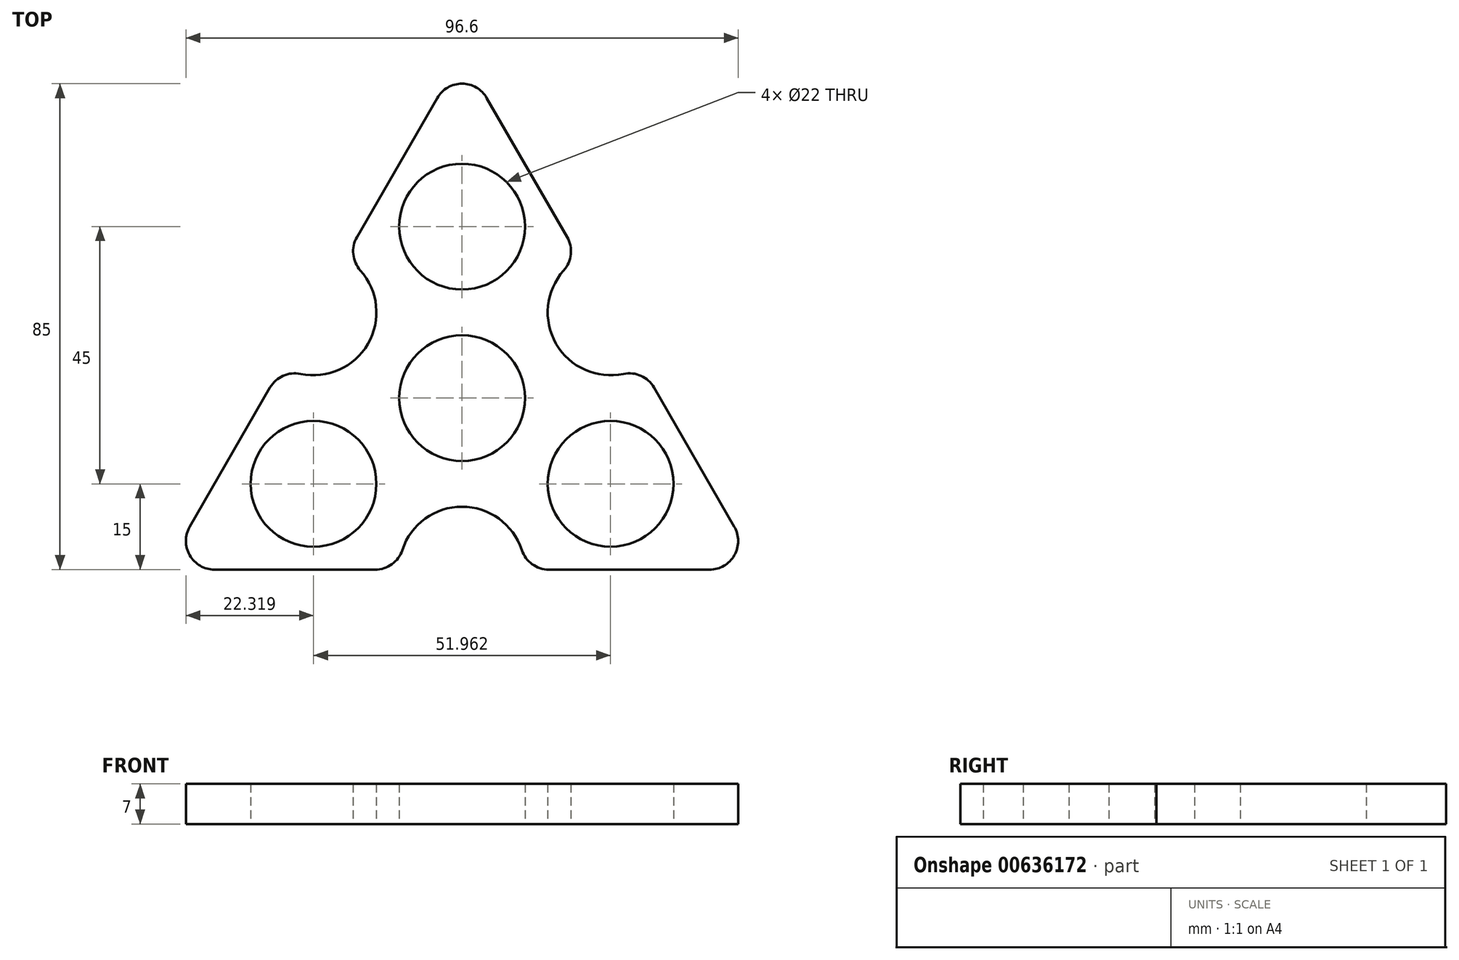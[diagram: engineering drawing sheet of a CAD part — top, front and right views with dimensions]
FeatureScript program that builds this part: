
annotation { "Feature Type Name" : "Feature", "Feature Type Description" : "" }
export const myFeature = defineFeature(function(context is Context, id is Id, definition is map)
    precondition{}
    {
        {
            var Q0;
            Q0=qCreatedBy(makeId("Top.planeOp"),FACE);
            var sketch = newSketch(context, id + "F0", { "sketchPlane" : qUnion([Q0])});
            skCircle(sketch, "E0", {"center": v(0, 0) * mm, "radius": 11 * mm});
            skCircle(sketch, "E1", {"center": v(0, 30) * mm, "radius": 11 * mm});
            skArc(sketch, "E2.1.0", {"start": v(-31.48, 5.47) * mm, "mid": v(-16.45, 9.5) * mm, "end": v(-20.48, 24.53) * mm});
            skCircle(sketch, "E2.2.0", {"center": v(-25.98, -15) * mm, "radius": 11 * mm});
            skArc(sketch, "E2.3.0", {"start": v(11, -30) * mm, "mid": v(0, -19) * mm, "end": v(-11, -30) * mm});
            skCircle(sketch, "E2.4.0", {"center": v(25.98, -15) * mm, "radius": 11 * mm});
            skArc(sketch, "E2.5.0", {"start": v(20.48, 24.53) * mm, "mid": v(16.45, 9.5) * mm, "end": v(31.48, 5.47) * mm});
            skLineSegment(sketch, "E3", {"start": v(-20.48, 24.53) * mm, "end": v(0, 60) * mm});
            skLineSegment(sketch, "E4", {"start": v(0, 60) * mm, "end": v(-20.48, 24.53) * mm});
            skLineSegment(sketch, "E5", {"start": v(0, 60) * mm, "end": v(20.48, 24.53) * mm});
            skLineSegment(sketch, "E6", {"start": v(-51.96, -30) * mm, "end": v(-11, -30) * mm});
            skLineSegment(sketch, "E7.trimOffspring", {"start": v(-31.48, 5.47) * mm, "end": v(-51.96, -30) * mm});
            skLineSegment(sketch, "E8.trimOffspring", {"start": v(31.48, 5.47) * mm, "end": v(51.96, -30) * mm});
            skLineSegment(sketch, "E9.trimOffspring", {"start": v(11, -30) * mm, "end": v(51.96, -30) * mm});
            skSolve(sketch);
        }
        {
            var Q0;
            Q0 = qSketchRegion(id + "F0", true);
            extrude(context, id + "F1", {"entities" : qUnion([Q0]), "depth" : 7 * mm, "offsetDistance" : 25 * mm});
        }
        {
            var Q0;
            Q0=makeQuery(id+"F1.opExtrude","SWEPT_EDGE",EDGE,{"disambiguationData":[OSD([sQuery(id+"F0.wireOp",EDGE,"E6"),sQuery(id+"F0.wireOp",EDGE,"E7.trimOffspring")])]});
            var Q1;
            Q1=makeQuery(id+"F1.opExtrude","SWEPT_EDGE",EDGE,{"disambiguationData":[OSD([sQuery(id+"F0.wireOp",EDGE,"E8.trimOffspring"),sQuery(id+"F0.wireOp",EDGE,"E9.trimOffspring")])]});
            var Q2;
            Q2=makeQuery(id+"F1.opExtrude","SWEPT_EDGE",EDGE,{"disambiguationData":[OSD([sQuery(id+"F0.wireOp",EDGE,"E4"),sQuery(id+"F0.wireOp",EDGE,"E5")])]});
            var Q3;
            Q3=makeQuery(id+"F1.opExtrude","SWEPT_EDGE",EDGE,{"disambiguationData":[OSD([sQuery(id+"F0.wireOp",EDGE,"E2.3.0"),sQuery(id+"F0.wireOp",EDGE,"E6")])]});
            var Q4;
            Q4=makeQuery(id+"F1.opExtrude","SWEPT_EDGE",EDGE,{"disambiguationData":[OSD([sQuery(id+"F0.wireOp",EDGE,"E2.3.0"),sQuery(id+"F0.wireOp",EDGE,"E9.trimOffspring")])]});
            var Q5;
            Q5=makeQuery(id+"F1.opExtrude","SWEPT_EDGE",EDGE,{"disambiguationData":[OSD([sQuery(id+"F0.wireOp",EDGE,"E2.5.0"),sQuery(id+"F0.wireOp",EDGE,"E8.trimOffspring")])]});
            var Q6;
            Q6=makeQuery(id+"F1.opExtrude","SWEPT_EDGE",EDGE,{"disambiguationData":[OSD([sQuery(id+"F0.wireOp",EDGE,"E2.5.0"),sQuery(id+"F0.wireOp",EDGE,"E5")])]});
            var Q7;
            Q7=makeQuery(id+"F1.opExtrude","SWEPT_EDGE",EDGE,{"disambiguationData":[OSD([sQuery(id+"F0.wireOp",EDGE,"E2.1.0"),sQuery(id+"F0.wireOp",EDGE,"E4")])]});
            var Q8;
            Q8=makeQuery(id+"F1.opExtrude","SWEPT_EDGE",EDGE,{"disambiguationData":[OSD([sQuery(id+"F0.wireOp",EDGE,"E2.1.0"),sQuery(id+"F0.wireOp",EDGE,"E7.trimOffspring")])]});
            fillet(context, id + "F2", {"entities" : qUnion([Q0, Q1, Q2, Q3, Q4, Q5, Q6, Q7, Q8]), "radius" : 5 * mm, "tangentPropagation" : true, "allowEdgeOverflow" : false});
        }
    });
